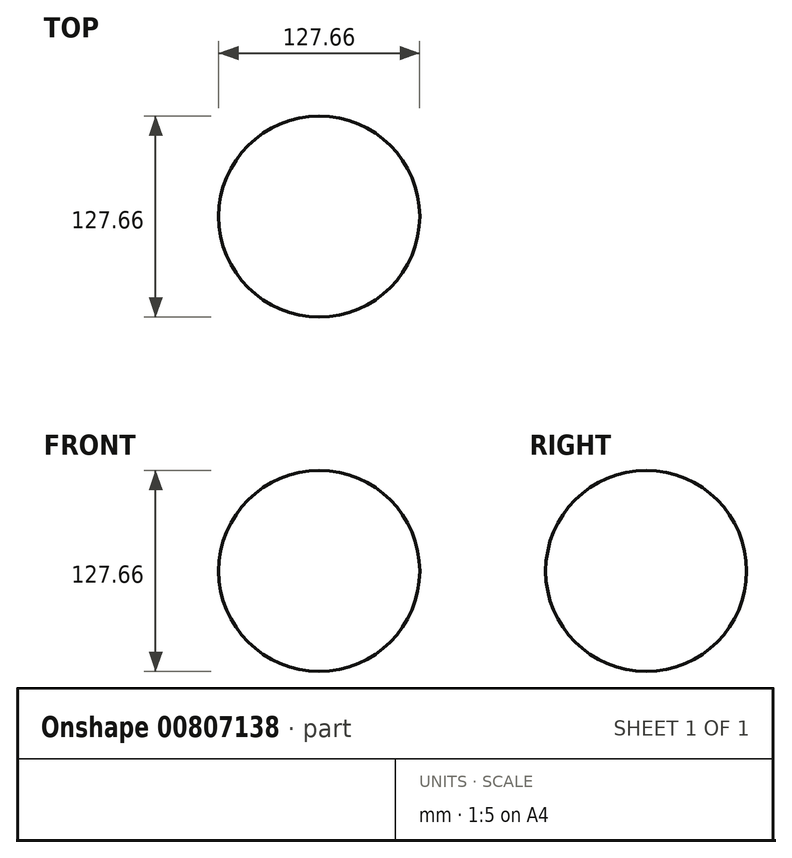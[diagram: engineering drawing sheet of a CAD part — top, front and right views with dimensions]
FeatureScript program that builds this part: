
annotation { "Feature Type Name" : "Feature", "Feature Type Description" : "" }
export const myFeature = defineFeature(function(context is Context, id is Id, definition is map)
    precondition{}
    {
        {
            var Q0;
            Q0=qCreatedBy(makeId("Front.planeOp"),FACE);
            var sketch = newSketch(context, id + "F0", { "sketchPlane" : qUnion([Q0])});
            skCircle(sketch, "E0", {"center": v(0, 0) * mm, "radius": 63.83 * mm});
            skLineSegment(sketch, "E1", {"start": v(-63.83, 0) * mm, "end": v(63.83, 0) * mm});
            skSolve(sketch);
        }
        {
            var Q0;
            {var subQ0=sQuery(id+"F0.wireOp",EDGE,"E1");Q0=makeQuery(id+"F0.imprint","IMPRINT",FACE,{"disambiguationData":[TD([[makeQuery(id+"F0.imprint","IMPRINT",EDGE,{"derivedFrom":subQ0}),-1.0]])]});}
            var Q1;
            Q1=sQuery(id+"F0.wireOp",EDGE,"E1");
            revolve(context, id + "F1", {"surfaceOperationType" : NewSurfaceOperationType.NEW, "entities" : qUnion([Q0]), "axis" : qUnion([Q1]), "revolveType" : RevolveType.FULL});
        }
    });
